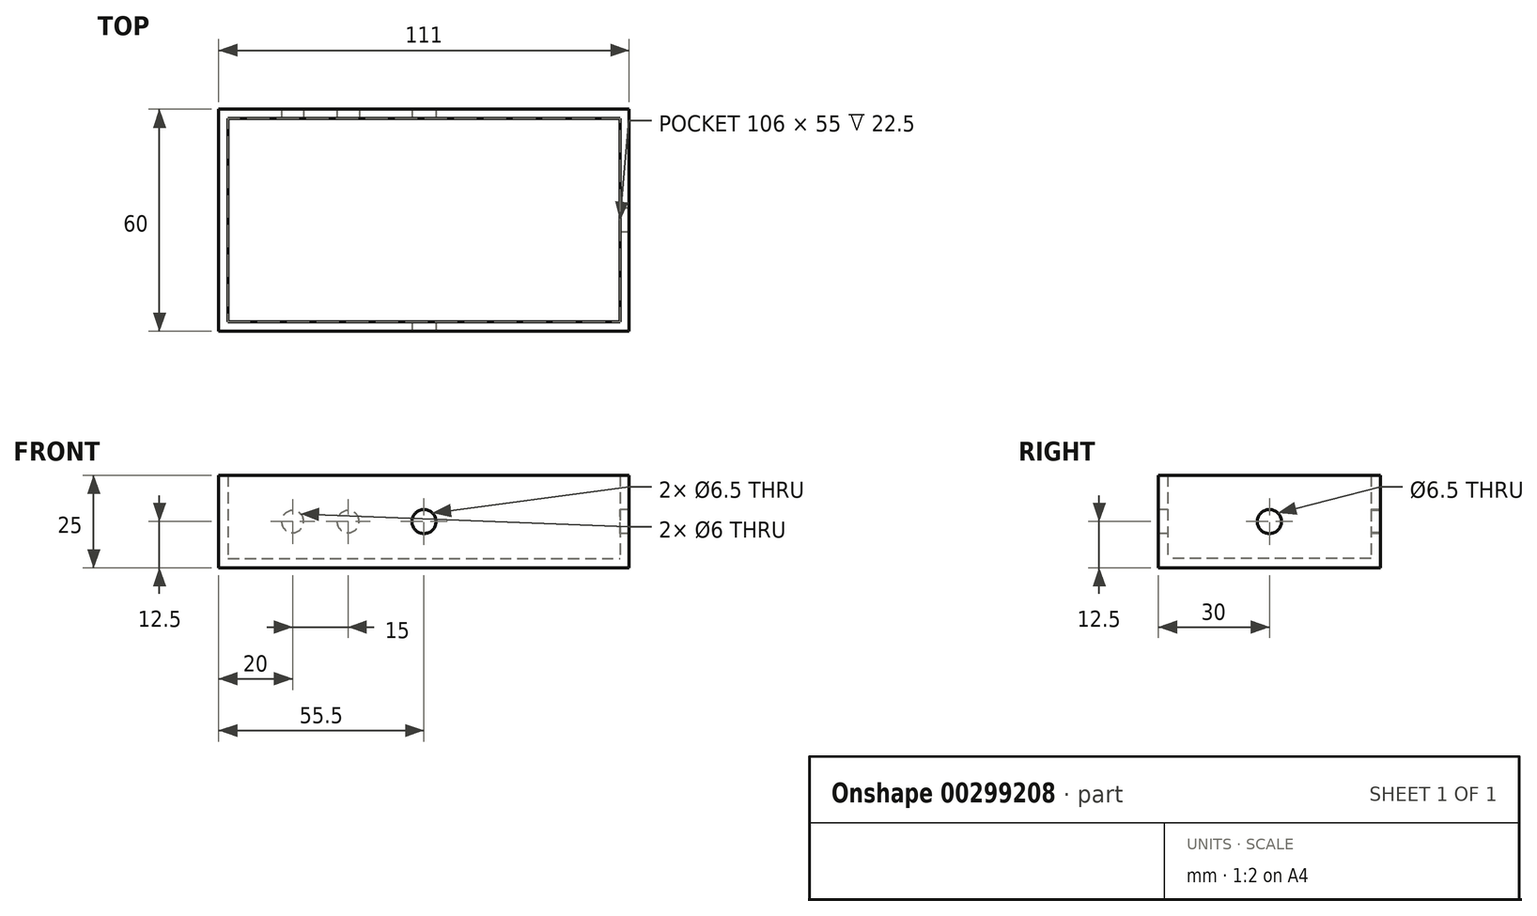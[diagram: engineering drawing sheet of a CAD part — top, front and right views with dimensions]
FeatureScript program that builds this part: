
annotation { "Feature Type Name" : "Feature", "Feature Type Description" : "" }
export const myFeature = defineFeature(function(context is Context, id is Id, definition is map)
    precondition{}
    {
        {
            var Q0;
            Q0=qCreatedBy(makeId("Top.planeOp"),FACE);
            var sketch = newSketch(context, id + "F0", { "sketchPlane" : qUnion([Q0])});
            skLineSegment(sketch, "E0.bottom", {"start": v(-55.5, 30) * mm, "end": v(55.5, 30) * mm});
            skLineSegment(sketch, "E0.top", {"start": v(-55.5, -30) * mm, "end": v(55.5, -30) * mm});
            skLineSegment(sketch, "E0.left", {"start": v(-55.5, 30) * mm, "end": v(-55.5, -30) * mm});
            skLineSegment(sketch, "E0.right", {"start": v(55.5, 30) * mm, "end": v(55.5, -30) * mm});
            skPoint(sketch, "E0.middle", {"position": v(0, 0) * mm});
            skSolve(sketch);
        }
        {
            var Q0;
            Q0 = qSketchRegion(id + "F0", true);
            extrude(context, id + "F1", {"entities" : qUnion([Q0]), "depth" : 25 * mm, "offsetDistance" : 25 * mm});
        }
        {
            var Q0;
            Q0=makeQuery(id+"F1.opExtrude","CAP_FACE",FACE,{"disambiguationData":[OSD([sQuery(id+"F0.wireOp",EDGE,"E0.bottom"),sQuery(id+"F0.wireOp",EDGE,"E0.top"),sQuery(id+"F0.wireOp",EDGE,"E0.left"),sQuery(id+"F0.wireOp",EDGE,"E0.right")])],"isStart":false});
            shell(context, id + "F2", {"entities" : qUnion([Q0]), "thickness" : 2.5 * mm});
        }
        {
            var Q0;
            Q0=qCreatedBy(makeId("Right.planeOp"),FACE);
            var sketch = newSketch(context, id + "F3", { "sketchPlane" : qUnion([Q0])});
            skCircle(sketch, "E1", {"center": v(0, 12.5) * mm, "radius": 3.25 * mm});
            skSolve(sketch);
        }
        {
            var Q0;
            Q0 = qSketchRegion(id + "F3", true);
            var Q1;
            Q1=makeQuery(id+"F1.opExtrude","SWEPT_FACE",FACE,{"disambiguationData":[OSD([sQuery(id+"F0.wireOp",EDGE,"E0.right")])]});
            extrude(context, id + "F4", {"entities" : qUnion([Q0]), "operationType" : NewBodyOperationType.REMOVE, "endBound" : BoundingType.UP_TO_SURFACE, "depth" : 25 * mm, "endBoundEntityFace" : qUnion([Q1]), "offsetDistance" : 25 * mm});
        }
        {
            var Q0;
            Q0=qCreatedBy(makeId("Front.planeOp"),FACE);
            var sketch = newSketch(context, id + "F5", { "sketchPlane" : qUnion([Q0])});
            skCircle(sketch, "E2", {"center": v(0, 12.5) * mm, "radius": 3.25 * mm});
            skSolve(sketch);
        }
        {
            var Q0;
            Q0 = qSketchRegion(id + "F5", true);
            var Q1;
            Q1=makeQuery(id+"F1.opExtrude","SWEPT_FACE",FACE,{"disambiguationData":[OSD([sQuery(id+"F0.wireOp",EDGE,"E0.bottom")])]});
            var Q2;
            Q2=makeQuery(id+"F1.opExtrude","SWEPT_FACE",FACE,{"disambiguationData":[OSD([sQuery(id+"F0.wireOp",EDGE,"E0.top")])]});
            extrude(context, id + "F6", {"entities" : qUnion([Q0]), "operationType" : NewBodyOperationType.REMOVE, "endBound" : BoundingType.UP_TO_SURFACE, "oppositeDirection" : true, "depth" : 25 * mm, "endBoundEntityFace" : qUnion([Q1]), "offsetDistance" : 25 * mm, "hasSecondDirection" : true, "secondDirectionBound" : SecondDirectionBoundingType.UP_TO_SURFACE, "secondDirectionOppositeDirection" : false, "secondDirectionDepth" : 25 * mm, "secondDirectionBoundEntityFace" : qUnion([Q2])});
        }
        {
            var Q0;
            Q0=qCreatedBy(makeId("Front.planeOp"),FACE);
            var sketch = newSketch(context, id + "F7", { "sketchPlane" : qUnion([Q0])});
            skCircle(sketch, "E3", {"center": v(-35.5, 12.5) * mm, "radius": 3 * mm});
            skCircle(sketch, "E4", {"center": v(-20.5, 12.5) * mm, "radius": 3 * mm});
            skSolve(sketch);
        }
        {
            var Q0;
            Q0 = qSketchRegion(id + "F7", true);
            var Q1;
            Q1=makeQuery(id+"F1.opExtrude","SWEPT_FACE",FACE,{"disambiguationData":[OSD([sQuery(id+"F0.wireOp",EDGE,"E0.bottom")])]});
            extrude(context, id + "F8", {"entities" : qUnion([Q0]), "operationType" : NewBodyOperationType.REMOVE, "endBound" : BoundingType.UP_TO_SURFACE, "oppositeDirection" : true, "depth" : 25 * mm, "endBoundEntityFace" : qUnion([Q1]), "offsetDistance" : 25 * mm});
        }
    });
